# Revit family: RBA2729-032
name_source: partatom
category: Plumbing Fixtures
revit_build: Autodesk Revit 2015 (Build: 20140223_1515(x64)
units: mm (PartAtom-declared; Revit-internal decimal feet)

## types (3) — shared parameters
Amperage = 4.6
CW Connection = Yes
CWFU = 1.5
Default Elevation = 838 mm
HW Connection = No
Manufacturer = RBA Group
Material = Stainless Steel Satin Finish
Modified Issue = 161020.01
URL = http://www.rba.com.au
Vent Connection = No
WFU = 2
Waste Connection = Yes
zero-valued in all types: HWFU

## per-type parameters (varying)
| type | Description | Model |
| rba2729-032 | 'Contour' Water Cooler, with Glass Filler 30 L/hr, 1.2mm type 304 Stainless Steel | rba2729-132 |
| rba2729-132 | 'Contour' Water Cooler, 30 L/hr, 1.2mm type 304 Stainless Steel | rba2729-032 |
| rba2729-833 | 'Contour' Heavy Duty Water Cooler, 30 L/hr, 2.0mm type 304 Stainless Steel | rba2729-833 |

## geometry (parser evidence)
native form markers: Blend x16, Sweep x8
no freeform markers — native parametric forms only
